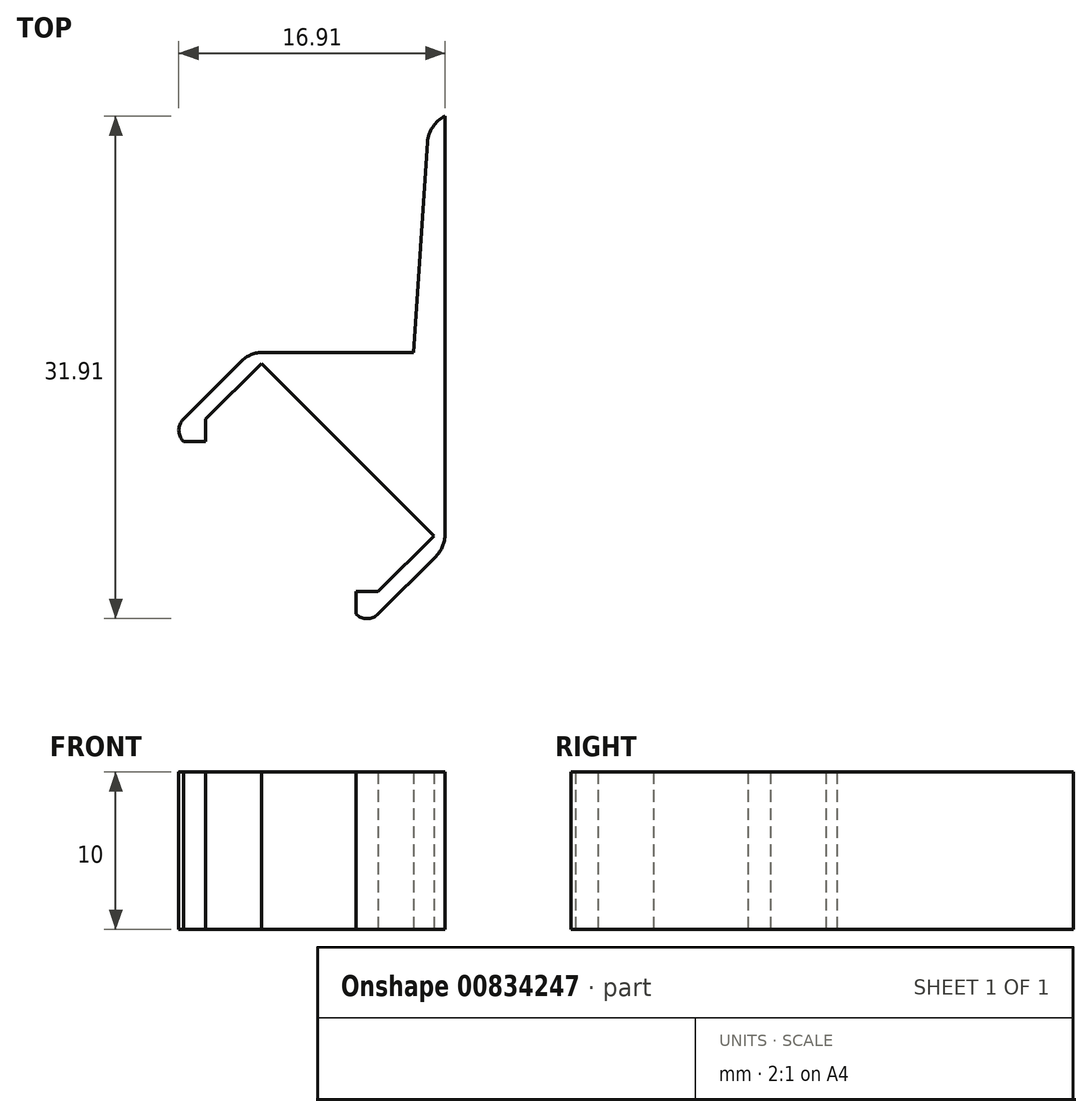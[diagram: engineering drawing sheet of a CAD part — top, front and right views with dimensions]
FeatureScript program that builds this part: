
annotation { "Feature Type Name" : "Feature", "Feature Type Description" : "" }
export const myFeature = defineFeature(function(context is Context, id is Id, definition is map)
    precondition{}
    {
        {
            var Q0;
            Q0=qCreatedBy(makeId("Top.planeOp"),FACE);
            var sketch = newSketch(context, id + "F0", { "sketchPlane" : qUnion([Q0])});
            skLineSegment(sketch, "E0", {"start": v(1, -22.5) * mm, "end": v(-11.37, -10.13) * mm, "construction": true});
            skLineSegment(sketch, "E1", {"start": v(1, -22.5) * mm, "end": v(1, 4.87) * mm});
            skLineSegment(sketch, "E2", {"start": v(1, 4.87) * mm, "end": v(0, 4.87) * mm});
            skLineSegment(sketch, "E3", {"start": v(0, 4.87) * mm, "end": v(-1, -10.13) * mm});
            skLineSegment(sketch, "E4", {"start": v(-1, -10.13) * mm, "end": v(-11.37, -10.13) * mm});
            skLineSegment(sketch, "E5", {"start": v(-11.37, -10.13) * mm, "end": v(-16.32, -15.08) * mm});
            skLineSegment(sketch, "E6", {"start": v(-16.32, -15.08) * mm, "end": v(-15.62, -15.8) * mm});
            skLineSegment(sketch, "E7", {"start": v(-15.62, -15.8) * mm, "end": v(-10.67, -10.84) * mm});
            skLineSegment(sketch, "E8", {"start": v(-10.67, -10.84) * mm, "end": v(0.3, -21.8) * mm});
            skLineSegment(sketch, "E9", {"start": v(0.3, -21.8) * mm, "end": v(-4.66, -26.75) * mm});
            skLineSegment(sketch, "E10", {"start": v(-4.66, -26.75) * mm, "end": v(-3.95, -27.46) * mm});
            skLineSegment(sketch, "E11", {"start": v(-3.95, -27.46) * mm, "end": v(1, -22.5) * mm});
            skLineSegment(sketch, "E12.bottom", {"start": v(-15.62, -15.8) * mm, "end": v(-14.2, -15.8) * mm});
            skLineSegment(sketch, "E12.top", {"start": v(-15.62, -14.38) * mm, "end": v(-14.2, -14.38) * mm});
            skLineSegment(sketch, "E12.left", {"start": v(-15.62, -15.8) * mm, "end": v(-15.62, -14.38) * mm});
            skLineSegment(sketch, "E12.right", {"start": v(-14.2, -15.8) * mm, "end": v(-14.2, -14.38) * mm});
            skLineSegment(sketch, "E13.bottom", {"start": v(-4.66, -26.75) * mm, "end": v(-3.24, -26.75) * mm});
            skLineSegment(sketch, "E13.top", {"start": v(-4.66, -25.34) * mm, "end": v(-3.24, -25.34) * mm});
            skLineSegment(sketch, "E13.left", {"start": v(-4.66, -26.75) * mm, "end": v(-4.66, -25.34) * mm});
            skLineSegment(sketch, "E13.right", {"start": v(-3.24, -26.75) * mm, "end": v(-3.24, -25.34) * mm});
            skSolve(sketch);
        }
        {
            var Q0;
            Q0 = qSketchRegion(id + "F0", true);
            extrude(context, id + "F1", {"entities" : qUnion([Q0]), "depth" : 10 * mm, "offsetDistance" : 25 * mm, "symmetric" : true});
        }
        {
            var Q0;
            Q0=makeQuery(id+"F1.opExtrude","SWEPT_EDGE",EDGE,{"disambiguationData":[OSD([sQuery(id+"F0.wireOp",EDGE,"E4"),sQuery(id+"F0.wireOp",EDGE,"E5")])]});
            var Q1;
            Q1=makeQuery(id+"F1.opExtrude","SWEPT_EDGE",EDGE,{"disambiguationData":[OSD([sQuery(id+"F0.wireOp",EDGE,"E1"),sQuery(id+"F0.wireOp",EDGE,"E11")])]});
            fillet(context, id + "F2", {"entities" : qUnion([Q0, Q1]), "radius" : 2 * mm, "tangentPropagation" : true, "allowEdgeOverflow" : false});
        }
        {
            var Q0;
            Q0=makeQuery(id+"F1.opExtrude","SWEPT_EDGE",EDGE,{"disambiguationData":[OSD([sQuery(id+"F0.wireOp",EDGE,"E5"),sQuery(id+"F0.wireOp",EDGE,"E6")])]});
            var Q1;
            Q1=makeQuery(id+"F1.opExtrude","SWEPT_EDGE",EDGE,{"disambiguationData":[OSD([sQuery(id+"F0.wireOp",EDGE,"E10"),sQuery(id+"F0.wireOp",EDGE,"E11")])]});
            fillet(context, id + "F3", {"entities" : qUnion([Q0, Q1]), "radius" : 1 * mm, "tangentPropagation" : true, "allowEdgeOverflow" : false});
        }
        {
            var Q0;
            Q0=makeQuery(id+"F1.opExtrude","SWEPT_EDGE",EDGE,{"disambiguationData":[OSD([sQuery(id+"F0.wireOp",EDGE,"E2"),sQuery(id+"F0.wireOp",EDGE,"E3")])]});
            fillet(context, id + "F4", {"entities" : qUnion([Q0]), "radius" : 2 * mm, "tangentPropagation" : true, "allowEdgeOverflow" : false});
        }
    });
